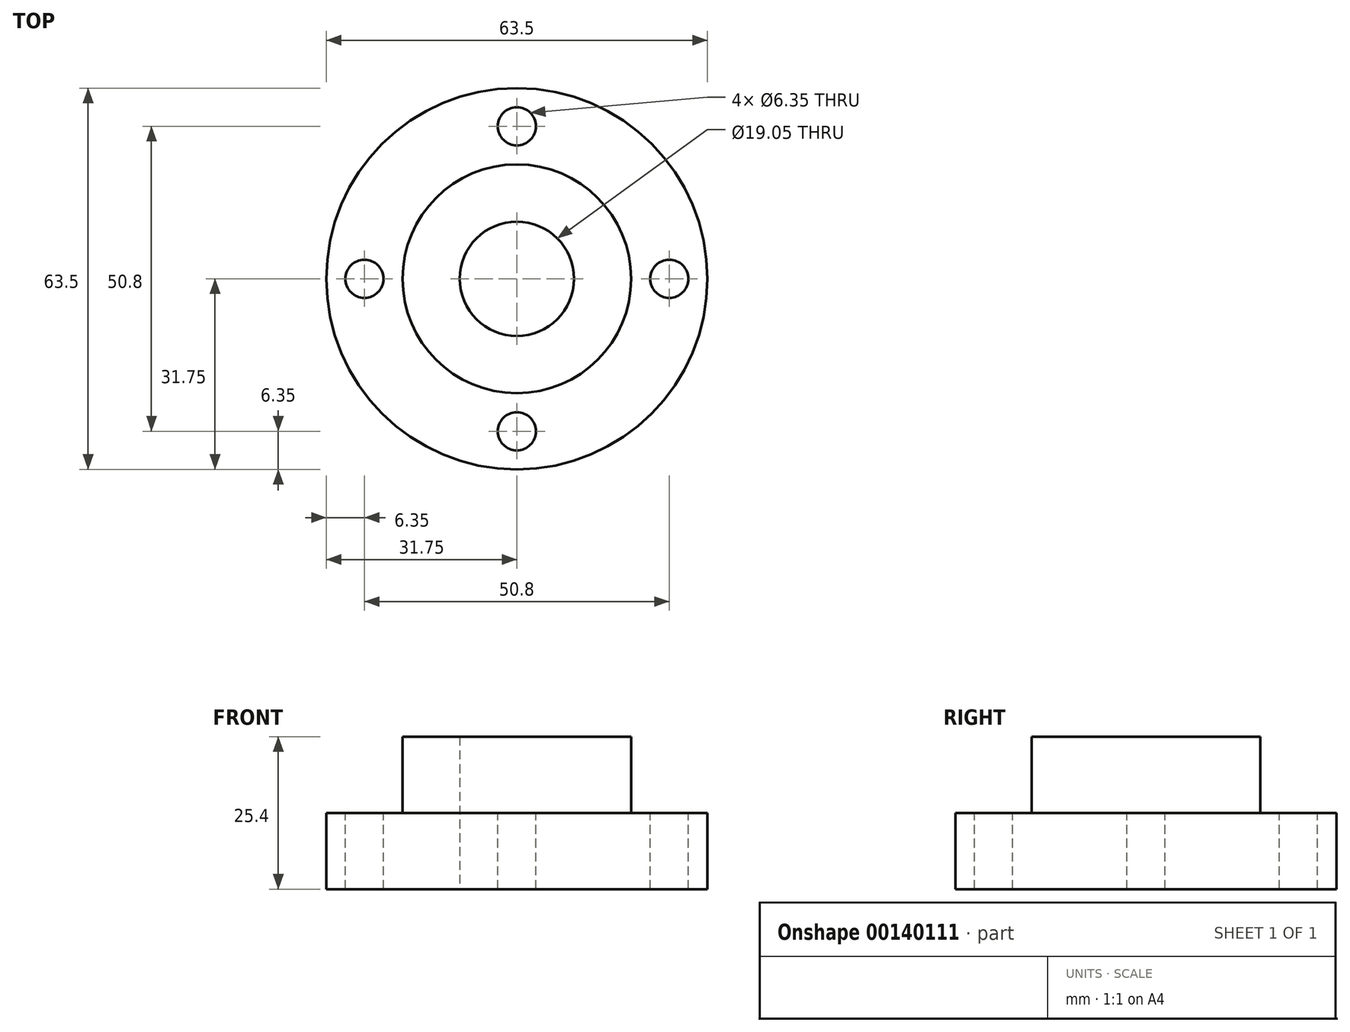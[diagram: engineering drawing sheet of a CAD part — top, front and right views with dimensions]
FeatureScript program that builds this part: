
annotation { "Feature Type Name" : "Feature", "Feature Type Description" : "" }
export const myFeature = defineFeature(function(context is Context, id is Id, definition is map)
    precondition{}
    {
        {
            var Q0;
            Q0=qCreatedBy(makeId("Top.planeOp"),FACE);
            var sketch = newSketch(context, id + "F0", { "sketchPlane" : qUnion([Q0])});
            skCircle(sketch, "E0", {"center": v(0, 0) * mm, "radius": 31.75 * mm});
            skCircle(sketch, "E1", {"center": v(0, 0) * mm, "radius": 19.05 * mm});
            skSolve(sketch);
        }
        {
            var Q0;
            Q0=makeQuery(id+"F0.imprint","IMPRINT",FACE,{"disambiguationData":[TD([[makeQuery(id+"F0.imprint","IMPRINT",EDGE,{"derivedFrom":sQuery(id+"F0.wireOp",EDGE,"E0")}),1.0]])]});
            extrude(context, id + "F1", {"entities" : qUnion([Q0]), "depth" : 12.7 * mm});
        }
        {
            var Q0;
            Q0=makeQuery(id+"F0.imprint","IMPRINT",FACE,{"disambiguationData":[TD([[makeQuery(id+"F0.imprint","IMPRINT",EDGE,{"derivedFrom":sQuery(id+"F0.wireOp",EDGE,"E1")}),1.0]])]});
            extrude(context, id + "F2", {"entities" : qUnion([Q0]), "operationType" : NewBodyOperationType.ADD, "depth" : 25.4 * mm});
        }
        {
            var Q0;
            Q0=sQuery(id+"F0.wireOp",VERTEX,"E0.center");
            var Q1;
            Q1=makeQuery(id+"F1.opExtrude","SWEPT_BODY",BODY,{"disambiguationData":[OSD([sQuery(id+"F0.wireOp",EDGE,"E0"),sQuery(id+"F0.wireOp",EDGE,"E1")])]});
            hole(context, id + "F3", {"style" : HoleStyle.SIMPLE, "endStyle" : HoleEndStyle.THROUGH, "oppositeDirection" : true, "holeDiameter" : 19.05 * mm, "locations" : qUnion([Q0]), "scope" : qUnion([Q1]), "isTappedThrough" : true});
        }
        {
            var Q0;
            Q0=makeQuery(id+"F1.opExtrude","CAP_FACE",FACE,{"disambiguationData":[OSD([sQuery(id+"F0.wireOp",EDGE,"E0"),sQuery(id+"F0.wireOp",EDGE,"E1")])],"isStart":false});
            var sketch = newSketch(context, id + "F4", { "sketchPlane" : qUnion([Q0])});
            skLineSegment(sketch, "E2", {"start": v(-31.75, 0) * mm, "end": v(-25.4, 0) * mm, "construction": true});
            skLineSegment(sketch, "E3", {"start": v(0, 31.75) * mm, "end": v(0, 25.4) * mm, "construction": true});
            skLineSegment(sketch, "E4.MirrorCS", {"start": v(0, -31.75) * mm, "end": v(0, -25.4) * mm, "construction": true});
            skLineSegment(sketch, "E5.MirrorCS", {"start": v(31.75, 0) * mm, "end": v(25.4, 0) * mm, "construction": true});
            skSolve(sketch);
        }
        {
            var Q0;
            Q0=sQuery(id+"F4.wireOp",VERTEX,"E3.end");
            var Q1;
            Q1=sQuery(id+"F4.wireOp",VERTEX,"E2.end");
            var Q2;
            Q2=sQuery(id+"F4.wireOp",VERTEX,"E4.MirrorCS.end");
            var Q3;
            Q3=sQuery(id+"F4.wireOp",VERTEX,"E5.MirrorCS.end");
            var Q4;
            Q4=makeQuery(id+"F1.opExtrude","SWEPT_BODY",BODY,{"disambiguationData":[OSD([sQuery(id+"F0.wireOp",EDGE,"E0"),sQuery(id+"F0.wireOp",EDGE,"E1")])]});
            hole(context, id + "F5", {"style" : HoleStyle.SIMPLE, "endStyle" : HoleEndStyle.THROUGH, "holeDiameter" : 6.35 * mm, "locations" : qUnion([Q0, Q1, Q2, Q3]), "scope" : qUnion([Q4]), "isTappedThrough" : true});
        }
    });
